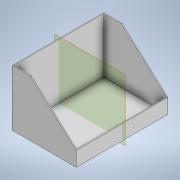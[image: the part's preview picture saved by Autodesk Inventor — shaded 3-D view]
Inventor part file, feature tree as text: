
AUTODESK INVENTOR PART (.ipt)
format: ipt  version: 2022 (Build 260153000, 153)  size: 135,680 bytes
history: native  units: in
note: dims shown in document units (in); Inventor stores cm internally (conversion verified against a paired STEP export)
features: extrude x4, sketch x4, plane x1, mirror x1
ambient origin geometry x8: Origin, YZ Plane, XZ Plane, XY Plane, X Axis, Y Axis, Z Axis, Center Point
bodies: Solid1 (feature_tree)
feature tree (10):
  extrude  "Extrusion1"  Depth=39.3701in
  extrude  "Extrusion2"  Depth=23.622in
  plane  "Work Plane1"
  mirror  "Mirror1"
  extrude  "Extrusion3"  Depth=5.9055in
  extrude  "Extrusion4"  Depth=0.3937in TaperAngle=0.0deg
  sketch  "Sketch2"  dims[d0=27.5591in d1=39.3701in]
  sketch  "Sketch3"  dims[d2=0.3937in d3=0.0in d4=23.622in]
  sketch  "Sketch4"  dims[d5=7.874in d6=5.9055in]
  sketch  "Sketch5"  dims[d7=0.3937in d8=0.0in d9=0.3937in d10=0.0in d11=0.3937in d12=0.0in d13=27.5591in d14=0.2885in]
